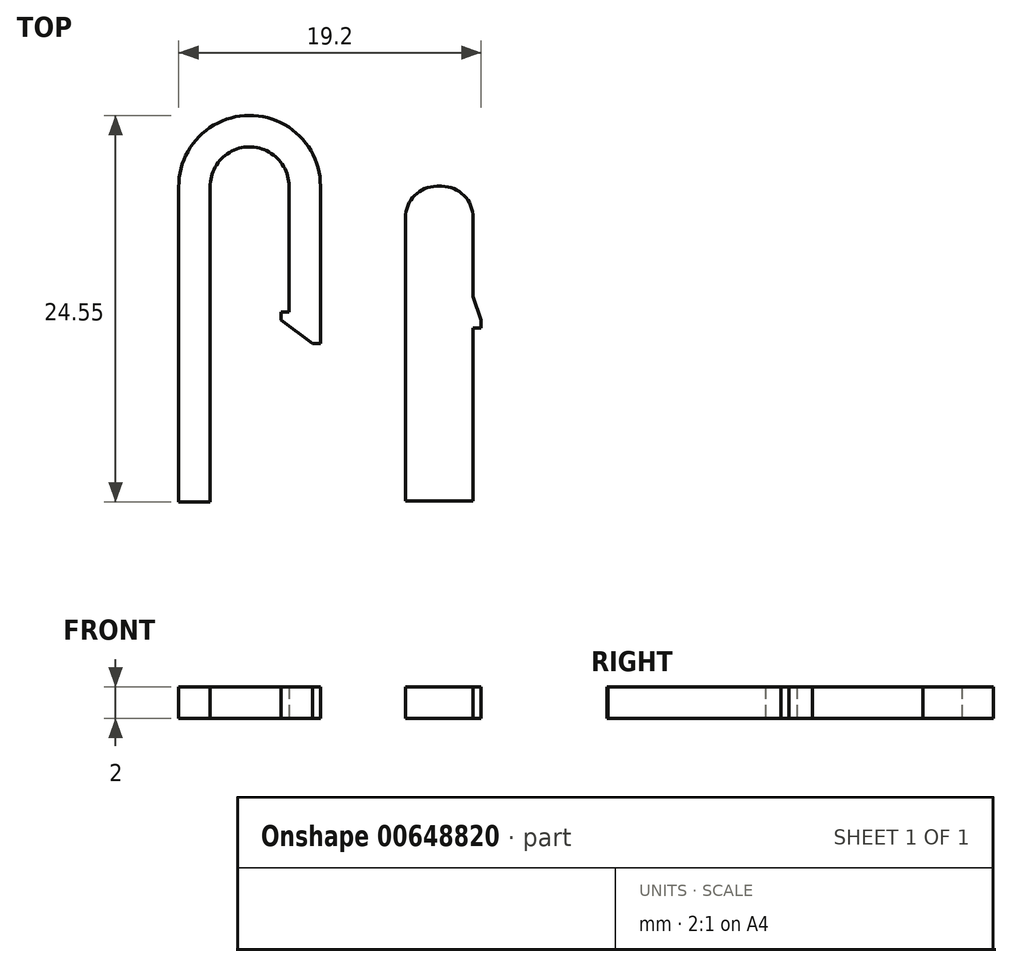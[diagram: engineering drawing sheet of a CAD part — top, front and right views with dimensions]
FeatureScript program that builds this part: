
annotation { "Feature Type Name" : "Feature", "Feature Type Description" : "" }
export const myFeature = defineFeature(function(context is Context, id is Id, definition is map)
    precondition{}
    {
        {
            var Q0;
            Q0=qCreatedBy(makeId("Top.planeOp"),FACE);
            var sketch = newSketch(context, id + "F0", { "sketchPlane" : qUnion([Q0])});
            skLineSegment(sketch, "E0.bottom", {"start": v(-36.48, 11.11) * mm, "end": v(-34.48, 11.11) * mm});
            skLineSegment(sketch, "E0.top", {"start": v(-36.48, -8.89) * mm, "end": v(-34.48, -8.89) * mm});
            skLineSegment(sketch, "E0.left", {"start": v(-36.48, 11.11) * mm, "end": v(-36.48, -8.89) * mm});
            skLineSegment(sketch, "E0.right", {"start": v(-34.48, 11.11) * mm, "end": v(-34.48, -8.89) * mm});
            skLineSegment(sketch, "E1.bottom", {"start": v(-29.48, 11.16) * mm, "end": v(-27.48, 11.16) * mm});
            skLineSegment(sketch, "E1.top", {"start": v(-29.48, 3.16) * mm, "end": v(-27.48, 3.16) * mm});
            skLineSegment(sketch, "E1.left", {"start": v(-29.48, 11.16) * mm, "end": v(-29.48, 3.16) * mm});
            skLineSegment(sketch, "E1.right", {"start": v(-27.48, 11.16) * mm, "end": v(-27.48, 3.16) * mm});
            skArc(sketch, "E2", {"start": v(-29.48, 11.16) * mm, "mid": v(-32, 13.66) * mm, "end": v(-34.48, 11.11) * mm});
            skArc(sketch, "E3", {"start": v(-27.48, 11.16) * mm, "mid": v(-32, 15.66) * mm, "end": v(-36.48, 11.11) * mm});
            skLineSegment(sketch, "E4.top", {"start": v(-27.48, 3.16) * mm, "end": v(-29.98, 3.16) * mm});
            skLineSegment(sketch, "E4.left", {"start": v(-27.48, 1.16) * mm, "end": v(-27.48, 3.16) * mm});
            skPoint(sketch, "E5", {"position": v(-27.98, 1.16) * mm});
            skPoint(sketch, "E6", {"position": v(-29.98, 2.66) * mm});
            skLineSegment(sketch, "E7", {"start": v(-27.98, 1.16) * mm, "end": v(-27.48, 1.16) * mm});
            skLineSegment(sketch, "E8", {"start": v(-29.98, 3.16) * mm, "end": v(-29.98, 2.66) * mm});
            skLineSegment(sketch, "E9", {"start": v(-29.98, 2.66) * mm, "end": v(-27.98, 1.16) * mm});
            skLineSegment(sketch, "E10.top", {"start": v(-27.98, 0.66) * mm, "end": v(-27.48, 0.66) * mm});
            skLineSegment(sketch, "E10.left", {"start": v(-27.98, 1.16) * mm, "end": v(-27.98, 0.66) * mm});
            skLineSegment(sketch, "E10.right", {"start": v(-27.48, 1.16) * mm, "end": v(-27.48, 0.66) * mm});
            skLineSegment(sketch, "E11.bottom", {"start": v(-22.08, 11.16) * mm, "end": v(-17.78, 11.16) * mm});
            skLineSegment(sketch, "E11.top", {"start": v(-22.08, -8.84) * mm, "end": v(-17.78, -8.84) * mm});
            skLineSegment(sketch, "E11.left", {"start": v(-22.08, 11.16) * mm, "end": v(-22.08, -8.84) * mm});
            skLineSegment(sketch, "E11.right", {"start": v(-17.78, 11.16) * mm, "end": v(-17.78, -8.84) * mm});
            skPoint(sketch, "E12", {"position": v(-17.78, 2.16) * mm});
            skPoint(sketch, "E13", {"position": v(-17.78, 4.16) * mm});
            skLineSegment(sketch, "E14", {"start": v(-17.78, 2.16) * mm, "end": v(-17.28, 2.16) * mm});
            skLineSegment(sketch, "E15", {"start": v(-17.28, 2.16) * mm, "end": v(-17.28, 2.66) * mm});
            skLineSegment(sketch, "E16", {"start": v(-17.28, 2.66) * mm, "end": v(-17.78, 4.16) * mm});
            skSolve(sketch);
        }
        {
            var Q0;
            Q0=makeQuery(id+"F0.imprint","IMPRINT",FACE,{"disambiguationData":[TD([[makeQuery(id+"F0.imprint","IMPRINT",EDGE,{"derivedFrom":sQuery(id+"F0.wireOp",EDGE,"E0.bottom")}),-1.0]])]});
            var Q1;
            Q1=makeQuery(id+"F0.imprint","IMPRINT",FACE,{"disambiguationData":[TD([[makeQuery(id+"F0.imprint","IMPRINT",EDGE,{"derivedFrom":sQuery(id+"F0.wireOp",EDGE,"E0.bottom")}),1.0]])]});
            var Q2;
            Q2=makeQuery(id+"F0.imprint","IMPRINT",FACE,{"disambiguationData":[TD([[makeQuery(id+"F0.imprint","IMPRINT",EDGE,{"derivedFrom":sQuery(id+"F0.wireOp",EDGE,"E1.bottom")}),-1.0]])]});
            var Q3;
            {var subQ1=sQuery(id+"F0.wireOp",EDGE,"E4.left");Q3=makeQuery(id+"F0.imprint","IMPRINT",FACE,{"disambiguationData":[TD([[makeQuery(id+"F0.imprint","IMPRINT",EDGE,{"derivedFrom":subQ1}),1.0]])]});}
            var Q4;
            Q4=makeQuery(id+"F0.imprint","IMPRINT",FACE,{"disambiguationData":[TD([[makeQuery(id+"F0.imprint","IMPRINT",EDGE,{"derivedFrom":sQuery(id+"F0.wireOp",EDGE,"E7")}),-1.0]])]});
            var Q5;
            {var subQ1=sQuery(id+"F0.wireOp",EDGE,"E11.bottom");Q5=makeQuery(id+"F0.imprint","IMPRINT",FACE,{"disambiguationData":[TD([[makeQuery(id+"F0.imprint","IMPRINT",EDGE,{"derivedFrom":subQ1}),-1.0]])]});}
            var Q6;
            {var subQ0=sQuery(id+"F0.wireOp",EDGE,"E14");Q6=makeQuery(id+"F0.imprint","IMPRINT",FACE,{"disambiguationData":[TD([[makeQuery(id+"F0.imprint","IMPRINT",EDGE,{"derivedFrom":subQ0}),1.0]])]});}
            extrude(context, id + "F1", {"entities" : qUnion([Q0, Q1, Q2, Q3, Q4, Q5, Q6]), "depth" : 2 * mm, "offsetDistance" : 25 * mm});
        }
        {
            var Q0;
            Q0=makeQuery(id+"F1.opExtrude","SWEPT_EDGE",EDGE,{"disambiguationData":[OSD([sQuery(id+"F0.wireOp",EDGE,"E11.bottom"),sQuery(id+"F0.wireOp",EDGE,"E11.right")])]});
            var Q1;
            Q1=makeQuery(id+"F1.opExtrude","SWEPT_EDGE",EDGE,{"disambiguationData":[OSD([sQuery(id+"F0.wireOp",EDGE,"E11.bottom"),sQuery(id+"F0.wireOp",EDGE,"E11.left")])]});
            fillet(context, id + "F2", {"entities" : qUnion([Q0, Q1]), "radius" : 2 * mm, "tangentPropagation" : true, "allowEdgeOverflow" : false});
        }
    });
